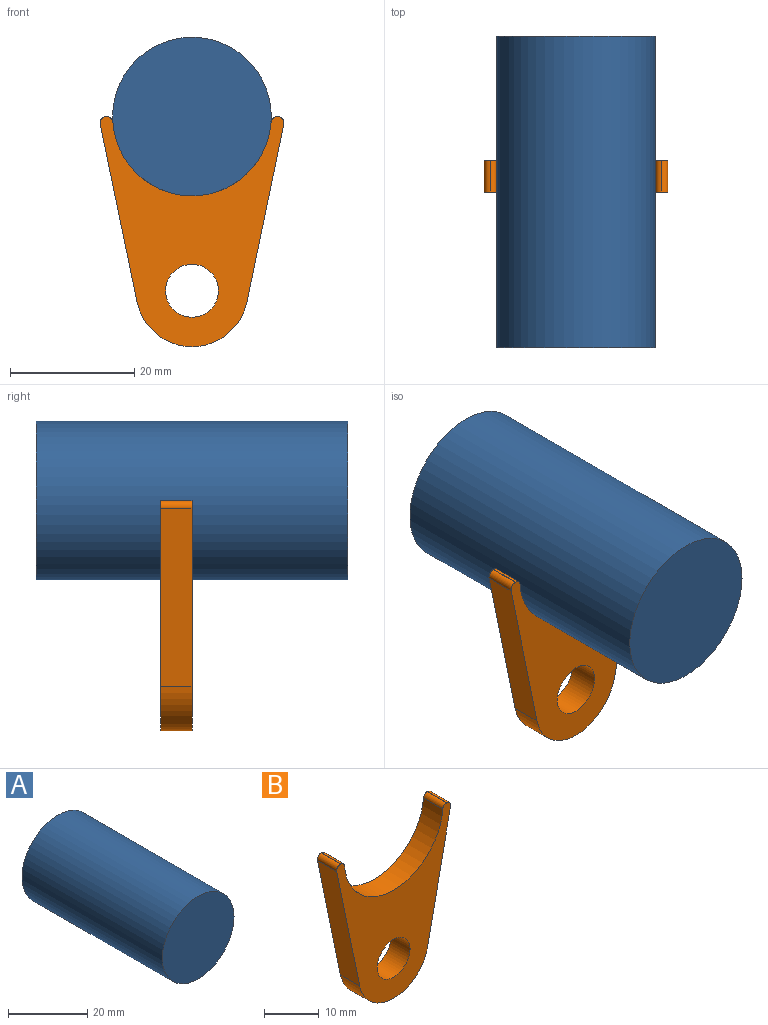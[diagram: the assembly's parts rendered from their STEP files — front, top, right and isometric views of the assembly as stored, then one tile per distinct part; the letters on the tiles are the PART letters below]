
ASSEMBLY  parts=2 mates=1
PART A: 3 faces, bbox 25.5x50x25.5 mm
  f0: cylinder r=12.75mm len=50mm, axis (0,1,0), area 4005.5mm2, adj f1,f2
  f1: plane 25.5x25.5mm, normal (0,-1,0), area 510.7mm2, adj f0
  f2: plane 25.5x25.5mm, normal (0,1,0), area 510.7mm2, adj f0
PART B: 13 faces, bbox 29.5x5x37 mm
  f0: plane 5x0.06mm, normal (0,0,1), area 0.3mm2, adj f6,f7,f9,f12
  f1: plane 28.63x5.94mm, normal (-0.98,0,-0.2), area 146.2mm2, adj f2,f6,f7,f9
  f2: cylinder r=9mm len=17.62mm, axis (0,1,0), area 123mm2, adj f1,f3,f6,f7
  f3: plane 28.63x5.94mm, normal (0.98,0,-0.2), area 146.2mm2, adj f2,f6,f7,f10
  f4: plane 5x0.06mm, normal (0,0,1), area 0.3mm2, adj f6,f7,f10,f11
  f5: cylinder r=12.75mm len=25.43mm, axis (0,1,0), area 191mm2, adj f6,f7,f11,f12
  f6: plane 37x29.54mm, normal (0,-1,0), area 491.7mm2, adj f0,f1,f2,f3,f4,f5,f8,f9
  f7: plane 37x29.54mm, normal (0,1,0), area 491.7mm2, adj f0,f1,f2,f3,f4,f5,f8,f9
  f8: cylinder r=4.25mm len=8.5mm, axis (0,-1,0), area 133.5mm2, adj f6,f7
  f9: cylinder r=1mm len=5mm, axis (0,1,0), area 8.9mm2, adj f0,f1,f6,f7
  f10: cylinder r=1mm len=5mm, axis (0,1,0), area 8.9mm2, adj f3,f4,f6,f7
  f11: cylinder r=1mm len=5mm, axis (0,1,0), area 7.5mm2, adj f4,f5,f6,f7
  f12: cylinder r=1mm len=5mm, axis (0,1,0), area 7.5mm2, adj f0,f5,f6,f7
PLACE A t=(-35.38,-11.33,0.1)mm
PLACE B t=(-35.38,-31.33,0.1)mm
MATE revolute B.f5 <-> A.f0  axis (0,-1,0) through (-35.38,-36.33,0.1)mm
